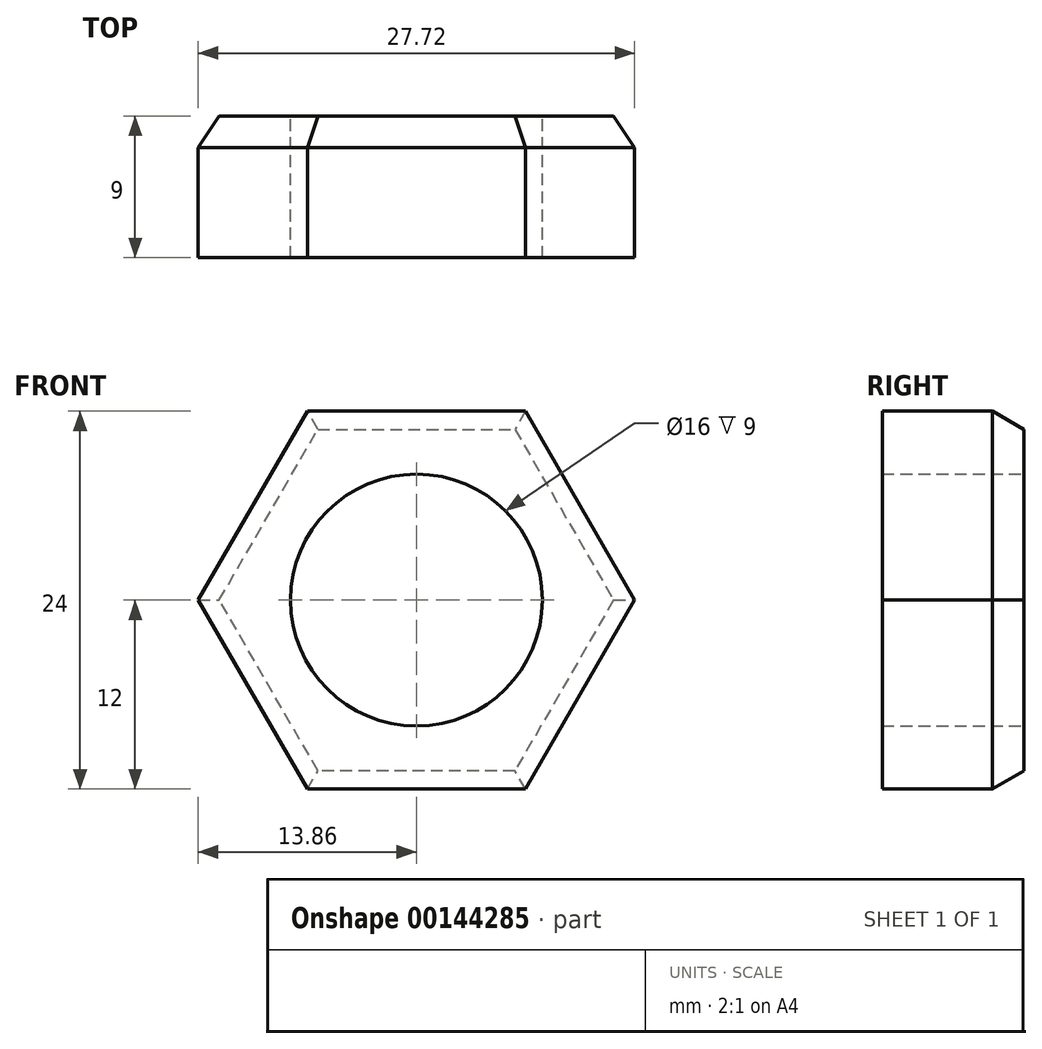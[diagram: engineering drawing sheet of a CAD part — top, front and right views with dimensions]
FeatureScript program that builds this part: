
annotation { "Feature Type Name" : "Feature", "Feature Type Description" : "" }
export const myFeature = defineFeature(function(context is Context, id is Id, definition is map)
    precondition{}
    {
        {
            var Q0;
            Q0=qCreatedBy(makeId("Front.planeOp"),FACE);
            var sketch = newSketch(context, id + "F0", { "sketchPlane" : qUnion([Q0])});
            skLineSegment(sketch, "E0", {"start": v(0, 0) * mm, "end": v(0, 12) * mm, "construction": true});
            skLineSegment(sketch, "E1", {"start": v(0, 0) * mm, "end": v(0, -12) * mm, "construction": true});
            skLineSegment(sketch, "E2", {"start": v(0, 0) * mm, "end": v(13.86, 0) * mm, "construction": true});
            skLineSegment(sketch, "E3", {"start": v(0, 0) * mm, "end": v(-13.86, 0) * mm, "construction": true});
            skLineSegment(sketch, "E4", {"start": v(-6.93, 12) * mm, "end": v(6.93, 12) * mm});
            skLineSegment(sketch, "E5", {"start": v(6.93, 12) * mm, "end": v(13.86, 0) * mm});
            skLineSegment(sketch, "E6", {"start": v(-6.93, -12) * mm, "end": v(6.93, -12) * mm});
            skLineSegment(sketch, "E7", {"start": v(6.93, -12) * mm, "end": v(13.86, 0) * mm});
            skLineSegment(sketch, "E8", {"start": v(-6.93, -12) * mm, "end": v(-13.86, 0) * mm});
            skLineSegment(sketch, "E9", {"start": v(-6.93, 12) * mm, "end": v(-13.86, 0) * mm});
            skCircle(sketch, "E10", {"center": v(0, 0) * mm, "radius": 8 * mm});
            skLineSegment(sketch, "E11", {"start": v(-13.86, 0) * mm, "end": v(6.93, 12) * mm, "construction": true});
            skLineSegment(sketch, "E12", {"start": v(13.86, 0) * mm, "end": v(-6.93, -12) * mm, "construction": true});
            skLineSegment(sketch, "E13", {"start": v(-6.93, 12) * mm, "end": v(6.93, -12) * mm, "construction": true});
            skSolve(sketch);
        }
        {
            var Q0;
            Q0=makeQuery(id+"F0.imprint","IMPRINT",FACE,{"disambiguationData":[TD([[makeQuery(id+"F0.imprint","IMPRINT",EDGE,{"derivedFrom":sQuery(id+"F0.wireOp",EDGE,"E4")}),-1.0]])]});
            extrude(context, id + "F1", {"entities" : qUnion([Q0]), "depth" : 9 * mm});
        }
        {
            var Q0;
            Q0=makeQuery(id+"F1.opExtrude","CAP_EDGE",EDGE,{"disambiguationData":[OSD([sQuery(id+"F0.wireOp",EDGE,"E9")])],"isStart":true});
            var Q1;
            Q1=makeQuery(id+"F1.opExtrude","CAP_EDGE",EDGE,{"disambiguationData":[OSD([sQuery(id+"F0.wireOp",EDGE,"E8")])],"isStart":true});
            var Q2;
            Q2=makeQuery(id+"F1.opExtrude","CAP_EDGE",EDGE,{"disambiguationData":[OSD([sQuery(id+"F0.wireOp",EDGE,"E4")])],"isStart":true});
            var Q3;
            Q3=makeQuery(id+"F1.opExtrude","CAP_EDGE",EDGE,{"disambiguationData":[OSD([sQuery(id+"F0.wireOp",EDGE,"E5")])],"isStart":true});
            var Q4;
            Q4=makeQuery(id+"F1.opExtrude","CAP_EDGE",EDGE,{"disambiguationData":[OSD([sQuery(id+"F0.wireOp",EDGE,"E7")])],"isStart":true});
            var Q5;
            Q5=makeQuery(id+"F1.opExtrude","CAP_EDGE",EDGE,{"disambiguationData":[OSD([sQuery(id+"F0.wireOp",EDGE,"E6")])],"isStart":true});
            chamfer(context, id + "F2", {"entities" : qUnion([Q0, Q1, Q2, Q3, Q4, Q5]), "chamferType" : ChamferType.OFFSET_ANGLE, "width" : 2 * mm, "oppositeDirection" : false, "angle" : 30 * degree, "tangentPropagation" : true});
        }
    });
